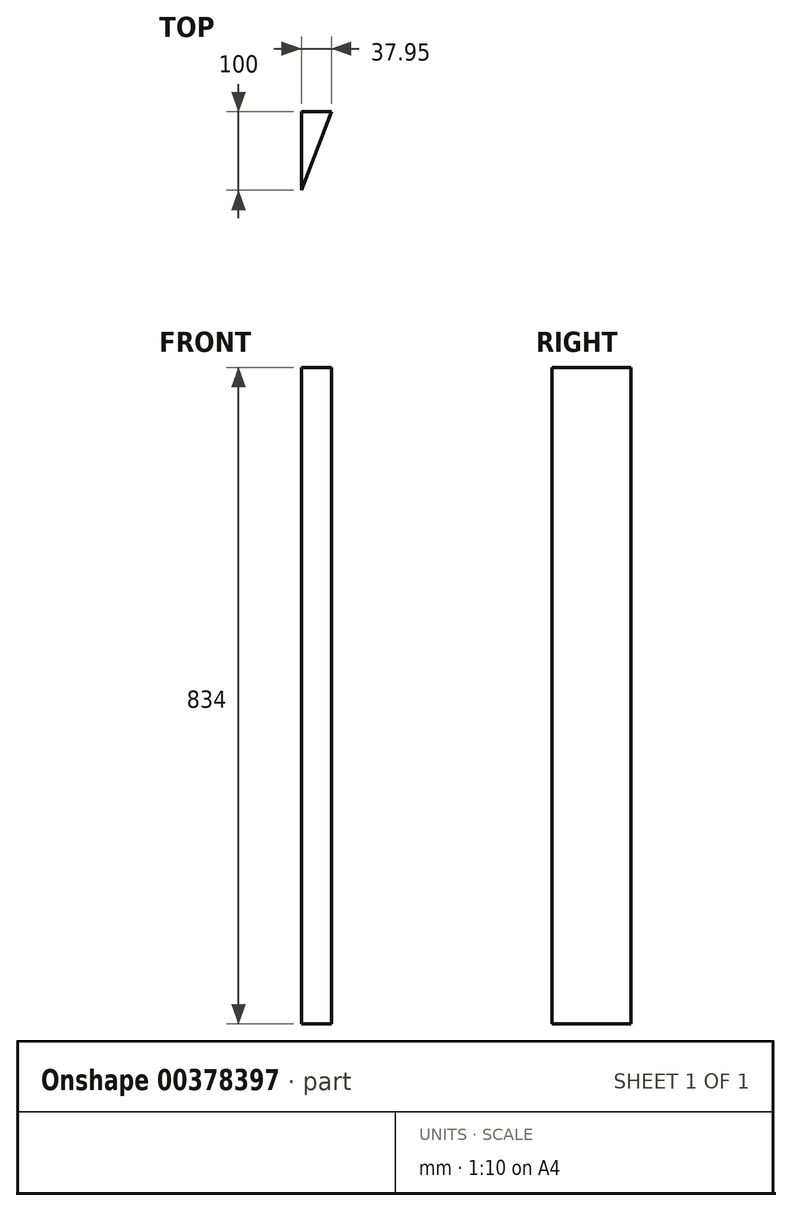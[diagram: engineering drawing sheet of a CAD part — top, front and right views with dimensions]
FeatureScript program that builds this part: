
annotation { "Feature Type Name" : "Feature", "Feature Type Description" : "" }
export const myFeature = defineFeature(function(context is Context, id is Id, definition is map)
    precondition{}
    {
        {
            var Q0;
            Q0=qCreatedBy(makeId("Top.planeOp"),FACE);
            var sketch = newSketch(context, id + "F0", { "sketchPlane" : qUnion([Q0])});
            skLineSegment(sketch, "E0", {"start": v(0, 0) * mm, "end": v(-37.95, -100) * mm});
            skLineSegment(sketch, "E1", {"start": v(-37.95, -100) * mm, "end": v(-37.95, 0) * mm});
            skLineSegment(sketch, "E2", {"start": v(-37.95, 0) * mm, "end": v(0, 0) * mm});
            skSolve(sketch);
        }
        {
            var Q0;
            Q0 = qSketchRegion(id + "F0", true);
            extrude(context, id + "F1", {"entities" : qUnion([Q0]), "depth" : 834 * mm});
        }
    });
